# Revit family: Gira_102400
name_source: partatom
category: Elektroinstallationen
revit_build: Autodesk Revit 2017 (Build: 20160225_1515(x64)
units: mm (PartAtom-declared; Revit-internal decimal feet)

## family parameters
Basisbauteil = Fläche
Beim Laden mit Abzugskörper schneiden = Nein
Bemaßung runder Anschluss = Durchmesser verwenden
Beschriftungsausrichtung beibehalten = Nein
Gemeinsam genutzt = Nein
Raumberechnungspunkt = Nein
Teiletyp = Normal

## types (1)
- Spannungsversorgung AC 24 V 1 A REG Zubehör
    Andere Bussysteme = ohne
    Anzahl der Ausgänge = 0
    Anzahl der binären Eingänge = 0
    BIM = https://media.stage.bim.site 8f.rfa
    BIMSITE_PRODUCT_ID = fb6a88596a59b92168ed2fe0f08236503b4a0cc7
    Beschreibung = Spannungsversorgung AC 24 V 1 A  REG Merkmale:  Spannungsversorgung für die Wetterstation und die eingebaute Heizung des Windsensors 0 - 10 V, Regensensor 0   10 V usw.
    Blindleistung = Nein
    Breite in Teilungseinheiten = 4
    Busspannung pufferbar = Nein
    Bussystem Funkbus = Nein
    Bussystem KNX = Nein
    Bussystem KNX-Funk = Nein
    Bussystem LON = Nein
    Bussystem Powernet = Nein
    Datenblatt = https://media.stage.bim.site
    Datenblatt 1 = https://media.stage.bim.site
    GTIN = 4010337010715
    Geeignet für C-Last = Nein
    HAN = 102400
    HeinzeBIM = https://www.heinze.de
    Hersteller = Gira
    Kosten = 0 $
    Max. Anzahl der Schaltausgänge = 0
    Mit Busankopplung = Nein
    Mit LED-Anzeige = Nein
    Montageart = REG
    Produktseite = https://media.stage.bim.site
    Tarifumschaltung = Nein
    Typname = Spannungsversorgung AC 24 V 1 A REG Zubehör
    URL = https://www.gira.de
    Vor Ort-/Handbedienung = Nein
    Vorgabe-Ansicht = 1219 mm
    Zulassung nach PTB = Nein

## geometry (parser evidence)
native form markers: Sweep x3
no freeform markers — native parametric forms only
